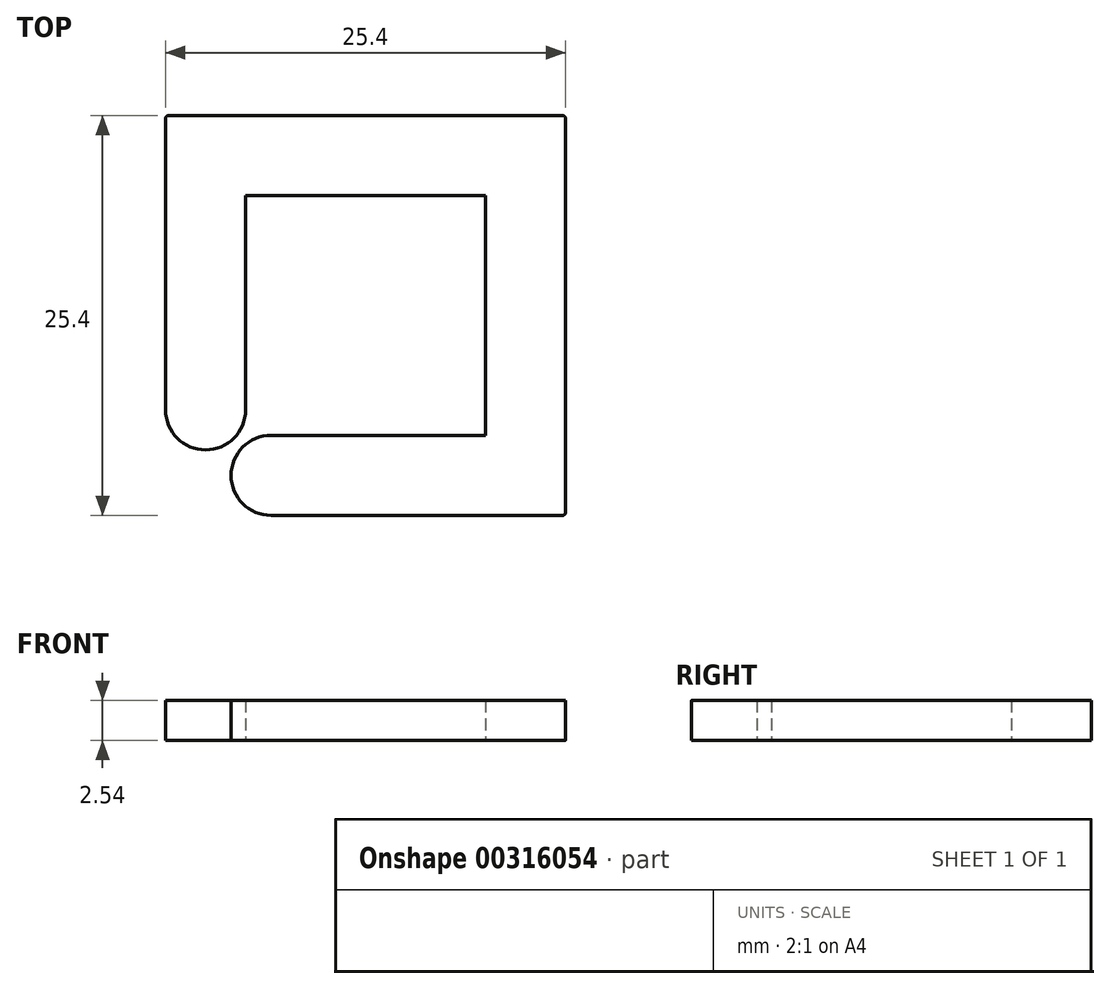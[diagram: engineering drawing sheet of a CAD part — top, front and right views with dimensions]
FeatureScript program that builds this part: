
annotation { "Feature Type Name" : "Feature", "Feature Type Description" : "" }
export const myFeature = defineFeature(function(context is Context, id is Id, definition is map)
    precondition{}
    {
        {
            var Q0;
            Q0=qCreatedBy(makeId("Top.planeOp"),FACE);
            var sketch = newSketch(context, id + "F0", { "sketchPlane" : qUnion([Q0])});
            skLineSegment(sketch, "E0.bottom", {"start": v(12.5, -12.7) * mm, "end": v(-6, -12.7) * mm});
            skLineSegment(sketch, "E0.top", {"start": v(12.5, 12.7) * mm, "end": v(-12.5, 12.7) * mm});
            skLineSegment(sketch, "E0.left", {"start": v(12.7, -12.5) * mm, "end": v(12.7, 12.5) * mm});
            skLineSegment(sketch, "E0.right", {"start": v(-12.7, -6) * mm, "end": v(-12.7, 12.5) * mm});
            skPoint(sketch, "E0.middle", {"position": v(0, 0) * mm});
            skLineSegment(sketch, "E1.0", {"start": v(-7.62, -6) * mm, "end": v(-7.62, 7.62) * mm});
            skLineSegment(sketch, "E1.1", {"start": v(7.62, -7.62) * mm, "end": v(-6, -7.62) * mm});
            skLineSegment(sketch, "E1.2", {"start": v(7.62, -7.62) * mm, "end": v(7.62, 7.62) * mm});
            skLineSegment(sketch, "E1.3", {"start": v(7.62, 7.62) * mm, "end": v(-7.62, 7.62) * mm});
            skPoint(sketch, "E2.visualSharp", {"position": v(-12.7, 12.7) * mm});
            skArc(sketch, "E2.filletArc", {"start": v(-12.5, 12.7) * mm, "mid": v(-12.64, 12.64) * mm, "end": v(-12.7, 12.5) * mm});
            skPoint(sketch, "E3.visualSharp", {"position": v(12.7, 12.7) * mm});
            skArc(sketch, "E3.filletArc", {"start": v(12.7, 12.5) * mm, "mid": v(12.64, 12.64) * mm, "end": v(12.5, 12.7) * mm});
            skPoint(sketch, "E4.visualSharp", {"position": v(12.7, -12.7) * mm});
            skArc(sketch, "E4.filletArc", {"start": v(12.5, -12.7) * mm, "mid": v(12.64, -12.64) * mm, "end": v(12.7, -12.5) * mm});
            skArc(sketch, "E5", {"start": v(-12.7, -6) * mm, "mid": v(-10.16, -8.54) * mm, "end": v(-7.62, -6) * mm});
            skPoint(sketch, "E6.center.orphan", {"position": v(-12.7, -12.7) * mm});
            skArc(sketch, "E7", {"start": v(-6, -7.62) * mm, "mid": v(-8.54, -10.16) * mm, "end": v(-6, -12.7) * mm});
            skLineSegment(sketch, "E8", {"start": v(-6, -12.7) * mm, "end": v(-6, -6) * mm, "construction": true});
            skLineSegment(sketch, "E9", {"start": v(-6, -6) * mm, "end": v(-12.7, -6) * mm, "construction": true});
            skSolve(sketch);
        }
        {
            var Q0;
            Q0 = qSketchRegion(id + "F0", true);
            extrude(context, id + "F1", {"entities" : qUnion([Q0]), "depth" : 2.54 * mm});
        }
    });
